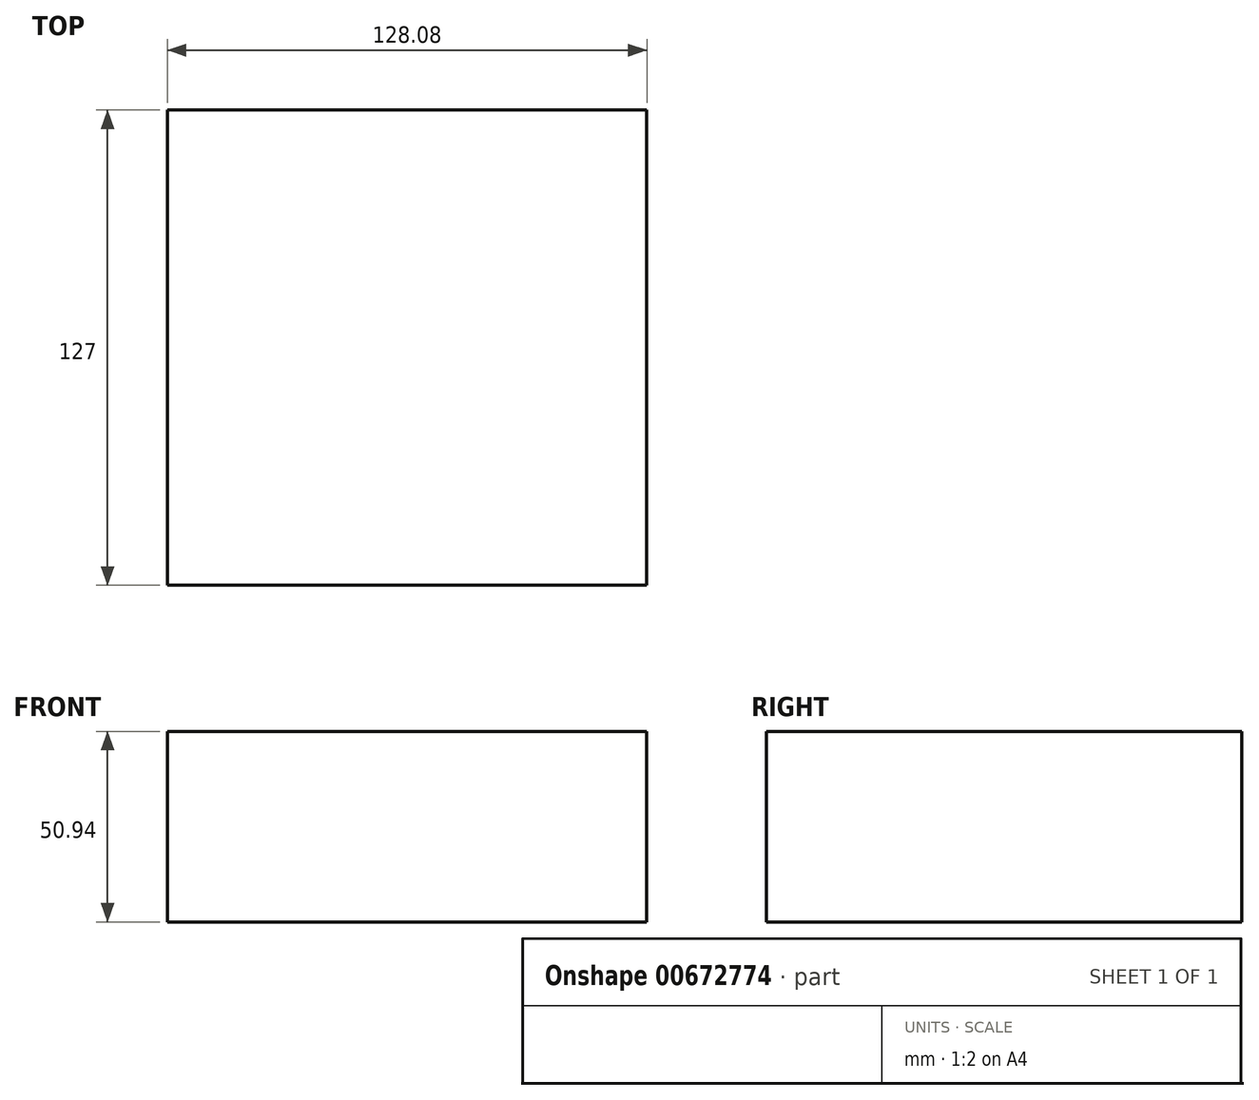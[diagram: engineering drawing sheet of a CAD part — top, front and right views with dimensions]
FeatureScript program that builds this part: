
annotation { "Feature Type Name" : "Feature", "Feature Type Description" : "" }
export const myFeature = defineFeature(function(context is Context, id is Id, definition is map)
    precondition{}
    {
        {
            var Q0;
            Q0=qCreatedBy(makeId("Front.planeOp"),FACE);
            var sketch = newSketch(context, id + "F0", { "sketchPlane" : qUnion([Q0])});
            skLineSegment(sketch, "E0.bottom", {"start": v(64.04, 25.47) * mm, "end": v(-64.04, 25.47) * mm});
            skLineSegment(sketch, "E0.top", {"start": v(64.04, -25.47) * mm, "end": v(-64.04, -25.47) * mm});
            skLineSegment(sketch, "E0.left", {"start": v(64.04, 25.47) * mm, "end": v(64.04, -25.47) * mm});
            skLineSegment(sketch, "E0.right", {"start": v(-64.04, 25.47) * mm, "end": v(-64.04, -25.47) * mm});
            skPoint(sketch, "E0.middle", {"position": v(0, 0) * mm});
            skLineSegment(sketch, "E1.bottom", {"start": v(-104.04, 68.93) * mm, "end": v(-47.63, 68.93) * mm});
            skLineSegment(sketch, "E1.top", {"start": v(-104.04, 83.9) * mm, "end": v(-47.63, 83.9) * mm});
            skLineSegment(sketch, "E1.left", {"start": v(-104.04, 68.93) * mm, "end": v(-104.04, 83.9) * mm});
            skLineSegment(sketch, "E1.right", {"start": v(-47.63, 68.93) * mm, "end": v(-47.63, 83.9) * mm});
            skPoint(sketch, "E1.middle", {"position": v(-75.84, 76.41) * mm});
            skLineSegment(sketch, "E2", {"start": v(-64.04, 25.47) * mm, "end": v(-16.96, 44.94) * mm});
            skArc(sketch, "E3", {"start": v(-16.96, 44.94) * mm, "mid": v(-6.56, 84.68) * mm, "end": v(-47.63, 83.9) * mm});
            skArc(sketch, "E4", {"start": v(-47.63, 83.9) * mm, "mid": v(-14.04, 46.36) * mm, "end": v(-29.22, 94.39) * mm});
            skSolve(sketch);
        }
        {
            var Q0;
            Q0=makeQuery(id+"F0.imprint","IMPRINT",FACE,{"disambiguationData":[TD([[makeQuery(id+"F0.imprint","IMPRINT",EDGE,{"derivedFrom":sQuery(id+"F0.wireOp",EDGE,"E0.bottom")}),1.0]])]});
            extrude(context, id + "F1", {"entities" : qUnion([Q0]), "endBound" : BoundingType.SYMMETRIC, "depth" : 127 * mm, "offsetDistance" : 25.4 * mm});
        }
    });
